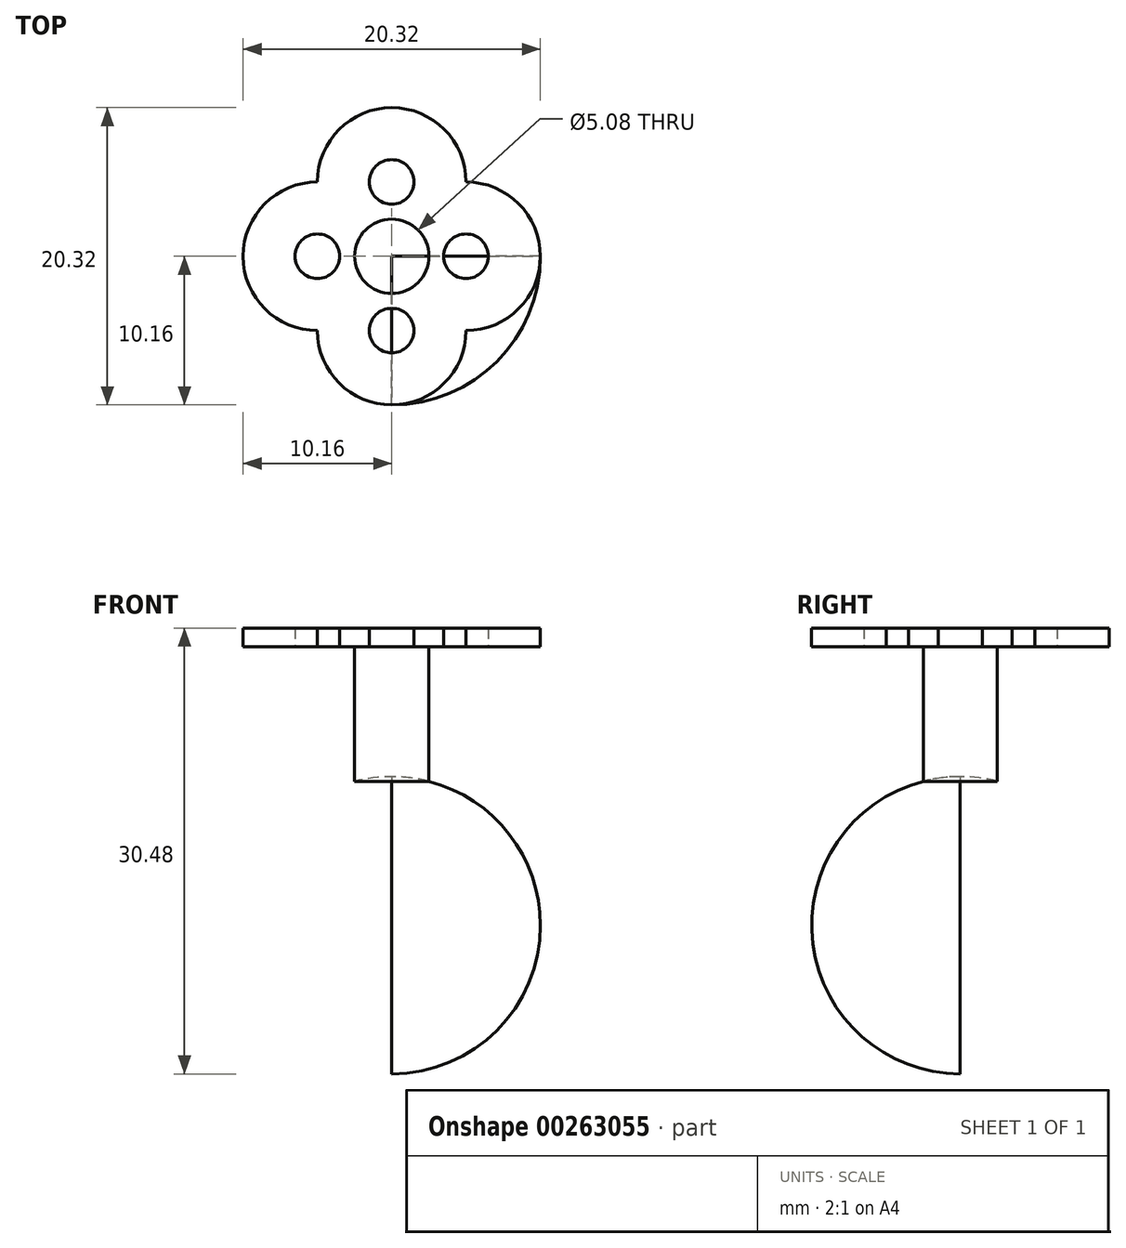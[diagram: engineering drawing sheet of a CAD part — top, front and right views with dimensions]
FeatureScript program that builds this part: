
annotation { "Feature Type Name" : "Feature", "Feature Type Description" : "" }
export const myFeature = defineFeature(function(context is Context, id is Id, definition is map)
    precondition{}
    {
        {
            var Q0;
            Q0=qCreatedBy(makeId("Top.planeOp"),FACE);
            var sketch = newSketch(context, id + "F0", { "sketchPlane" : qUnion([Q0])});
            skArc(sketch, "E0", {"start": v(-10.16, 0) * mm, "mid": v(0, -10.16) * mm, "end": v(10.16, 0) * mm});
            skLineSegment(sketch, "E1", {"start": v(-10.16, 0) * mm, "end": v(10.16, 0) * mm});
            skSolve(sketch);
        }
        {
            var Q0;
            Q0=qCreatedBy(makeId("Right.planeOp"),FACE);
            var sketch = newSketch(context, id + "F1", { "sketchPlane" : qUnion([Q0])});
            skCircle(sketch, "E2", {"center": v(0, 0) * mm, "radius": 3.81 * mm});
            skSolve(sketch);
        }
        {
            var Q0;
            Q0=makeQuery(id+"F0.imprint","IMPRINT",FACE,{"disambiguationData":[TD([[makeQuery(id+"F0.imprint","IMPRINT",EDGE,{"derivedFrom":sQuery(id+"F0.wireOp",EDGE,"E0")}),1.0]])]});
            var Q1;
            Q1=sQuery(id+"F1.wireOp",EDGE,"E2");
            revolve(context, id + "F2", {"entities" : qUnion([Q0]), "axis" : qUnion([Q1]), "revolveType" : RevolveType.FULL});
        }
        {
            var Q0;
            Q0=qCreatedBy(makeId("Top.planeOp"),FACE);
            var sketch = newSketch(context, id + "F3", { "sketchPlane" : qUnion([Q0])});
            skCircle(sketch, "E3", {"center": v(0, 0) * mm, "radius": 2.54 * mm});
            skSolve(sketch);
        }
        {
            var Q0;
            Q0 = qSketchRegion(id + "F3", true);
            extrude(context, id + "F4", {"entities" : qUnion([Q0]), "operationType" : NewBodyOperationType.ADD, "depth" : 19.05 * mm});
        }
        {
            var Q0;
            Q0=makeQuery(id+"F4.opExtrude","CAP_FACE",FACE,{"disambiguationData":[OSD([sQuery(id+"F3.wireOp",EDGE,"E3")])],"isStart":false});
            var sketch = newSketch(context, id + "F5", { "sketchPlane" : qUnion([Q0])});
            skLineSegment(sketch, "E4.bottom", {"start": v(5.08, 5.08) * mm, "end": v(-5.08, 5.08) * mm, "construction": true});
            skLineSegment(sketch, "E4.top", {"start": v(5.08, -5.08) * mm, "end": v(-5.08, -5.08) * mm, "construction": true});
            skLineSegment(sketch, "E4.left", {"start": v(5.08, 5.08) * mm, "end": v(5.08, -5.08) * mm, "construction": true});
            skLineSegment(sketch, "E4.right", {"start": v(-5.08, 5.08) * mm, "end": v(-5.08, -5.08) * mm, "construction": true});
            skPoint(sketch, "E4.middle", {"position": v(0, 0) * mm});
            skArc(sketch, "E5", {"start": v(-5.08, 5.08) * mm, "mid": v(-10.16, 0) * mm, "end": v(-5.08, -5.08) * mm});
            skArc(sketch, "E6", {"start": v(5.08, 5.08) * mm, "mid": v(0, 10.16) * mm, "end": v(-5.08, 5.08) * mm});
            skArc(sketch, "E7", {"start": v(-5.08, -5.08) * mm, "mid": v(0, -10.16) * mm, "end": v(5.08, -5.08) * mm});
            skArc(sketch, "E8", {"start": v(5.08, -5.08) * mm, "mid": v(10.16, 0) * mm, "end": v(5.08, 5.08) * mm});
            skCircle(sketch, "E9", {"center": v(-5.08, 0) * mm, "radius": 1.52 * mm});
            skCircle(sketch, "E10", {"center": v(0, 5.08) * mm, "radius": 1.52 * mm});
            skCircle(sketch, "E11", {"center": v(5.08, 0) * mm, "radius": 1.52 * mm});
            skCircle(sketch, "E12", {"center": v(0, -5.08) * mm, "radius": 1.52 * mm});
            skSolve(sketch);
        }
        {
            var Q0;
            Q0 = qSketchRegion(id + "F5", true);
            extrude(context, id + "F6", {"entities" : qUnion([Q0]), "operationType" : NewBodyOperationType.ADD, "depth" : 1.27 * mm});
        }
        {
            var Q0;
            Q0=qCreatedBy(makeId("Right.planeOp"),FACE);
            var sketch = newSketch(context, id + "F7", { "sketchPlane" : qUnion([Q0])});
            skArc(sketch, "E13", {"start": v(0, 10.16) * mm, "mid": v(-10.16, 0) * mm, "end": v(0, -10.16) * mm});
            skLineSegment(sketch, "E14", {"start": v(0, 10.16) * mm, "end": v(0, -10.16) * mm});
            skSolve(sketch);
        }
        {
            var Q0;
            Q0=qCreatedBy(makeId("Top.planeOp"),FACE);
            var sketch = newSketch(context, id + "F8", { "sketchPlane" : qUnion([Q0])});
            skCircle(sketch, "E15", {"center": v(0, 0) * mm, "radius": 4.45 * mm});
            skSolve(sketch);
        }
        {
            var Q0;
            Q0 = qSketchRegion(id + "F7", true);
            var Q1;
            Q1=sQuery(id+"F8.wireOp",EDGE,"E15");
            revolve(context, id + "F9", {"operationType" : NewBodyOperationType.REMOVE, "entities" : qUnion([Q0]), "axis" : qUnion([Q1]), "revolveType" : RevolveType.ONE_DIRECTION, "angle" : 90 * degree});
        }
    });
